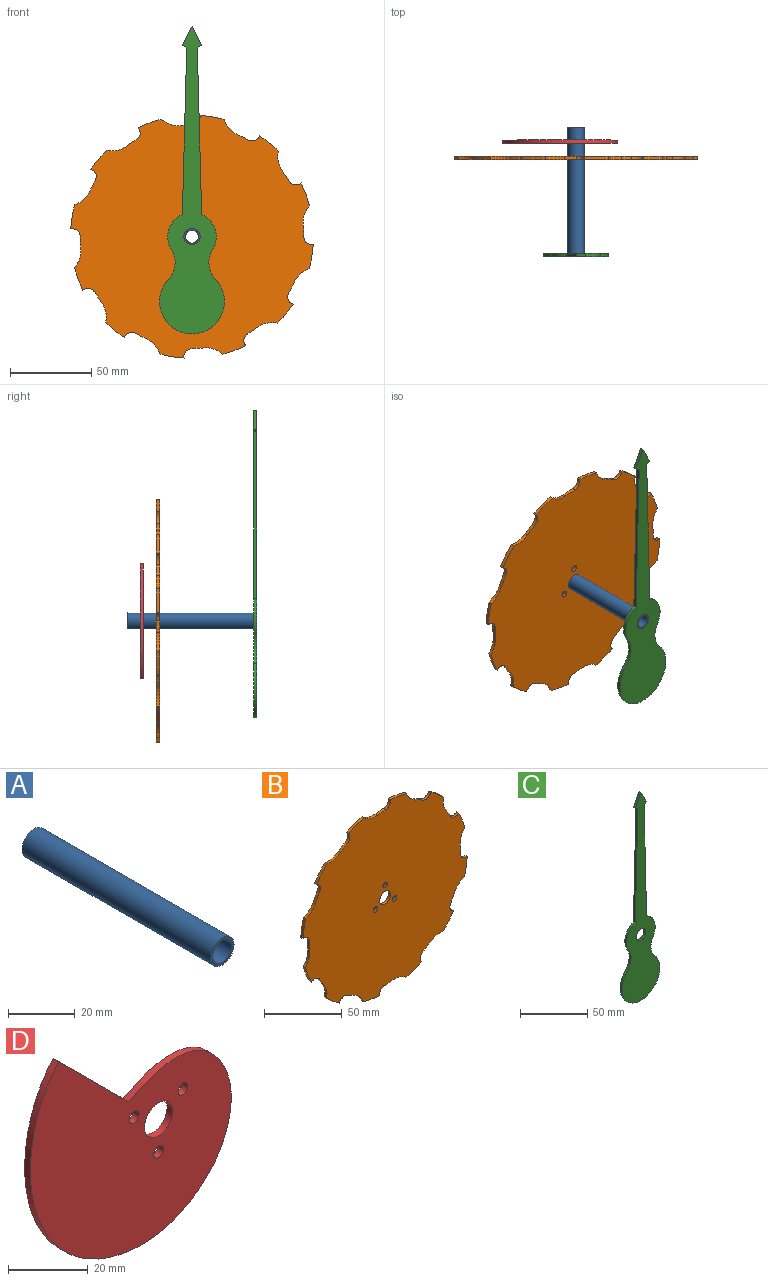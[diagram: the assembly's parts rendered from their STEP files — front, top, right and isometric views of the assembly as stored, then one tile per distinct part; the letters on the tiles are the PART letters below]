
ASSEMBLY  parts=4 mates=3
PART A: 4 faces, bbox 10x80x10 mm
  f0: cylinder r=4mm len=80mm, axis (0,1,0), area 2010.6mm2, adj f2,f3
  f1: cylinder r=5mm len=80mm, axis (0,1,0), area 2513.3mm2, adj f2,f3
  f2: plane 10x10mm, normal (0,-1,0), area 28.3mm2, adj f0,f1
  f3: plane 10x10mm, normal (0,1,0), area 28.3mm2, adj f0,f1
PART B: 54 faces, bbox 149.7x2x149.7 mm
  f0: cylinder r=75mm len=11.65mm, axis (0,1,0), area 30.3mm2, adj f13,f14,f47,f48
  f1: cylinder r=75mm len=14.9mm, axis (0,1,0), area 30.3mm2, adj f13,f14,f44,f45
  f2: cylinder r=75mm len=14.16mm, axis (0,1,0), area 30.3mm2, adj f13,f14,f41,f42
  f3: cylinder r=75mm len=11.65mm, axis (0,1,0), area 30.3mm2, adj f13,f14,f38,f39
  f4: cylinder r=75mm len=14.9mm, axis (0,1,0), area 30.3mm2, adj f13,f14,f35,f36
  f5: cylinder r=75mm len=14.16mm, axis (0,1,0), area 30.3mm2, adj f13,f14,f32,f33
  f6: cylinder r=75mm len=11.65mm, axis (0,1,0), area 30.3mm2, adj f13,f14,f29,f30
  f7: cylinder r=75mm len=14.9mm, axis (0,1,0), area 30.3mm2, adj f13,f14,f17,f27
  f8: cylinder r=75mm len=14.16mm, axis (0,1,0), area 30.3mm2, adj f13,f14,f24,f50
  f9: cylinder r=75mm len=14.9mm, axis (0,1,0), area 30.3mm2, adj f13,f14,f21,f26
  f10: cylinder r=75mm len=11.65mm, axis (0,1,0), area 30.3mm2, adj f13,f14,f18,f23
  f11: cylinder r=5mm len=10mm, axis (0,1,0), area 62.8mm2, adj f13,f14
  f12: cylinder r=75mm len=14.16mm, axis (0,1,0), area 30.3mm2, adj f13,f14,f15,f20
  f13: plane 149.68x149.68mm, normal (0,-1,0), area 16158.8mm2, adj f0,f1,f2,f3,f4,f5,f6,f7
  f14: plane 149.68x149.68mm, normal (0,1,0), area 16158.8mm2, adj f0,f1,f2,f3,f4,f5,f6,f7
  f15: cylinder r=15mm len=11.78mm, axis (0,-1,0), area 25.6mm2, adj f12,f13,f14,f16
  f16: cylinder r=69mm len=7.21mm, axis (0,-1,0), area 14.5mm2, adj f13,f14,f15,f17
  f17: cylinder r=5mm len=5.84mm, axis (0,-1,0), area 17.4mm2, adj f7,f13,f14,f16
  f18: cylinder r=15mm len=12.17mm, axis (0,-1,0), area 25.6mm2, adj f10,f13,f14,f19
  f19: cylinder r=69mm len=6.06mm, axis (0,-1,0), area 14.5mm2, adj f13,f14,f18,f20
  f20: cylinder r=5mm len=7.52mm, axis (0,-1,0), area 17.4mm2, adj f12,f13,f14,f19
  f21: cylinder r=15mm len=9.3mm, axis (0,-1,0), area 25.6mm2, adj f9,f13,f14,f22
  f22: cylinder r=69mm len=6.44mm, axis (0,-1,0), area 14.5mm2, adj f13,f14,f21,f23
  f23: cylinder r=5mm len=7.19mm, axis (0,-1,0), area 17.4mm2, adj f10,f13,f14,f22
  f24: cylinder r=15mm len=11.78mm, axis (0,-1,0), area 25.6mm2, adj f8,f13,f14,f25
  f25: cylinder r=69mm len=7.21mm, axis (0,-1,0), area 14.5mm2, adj f13,f14,f24,f26
  f26: cylinder r=5mm len=5.84mm, axis (0,-1,0), area 17.4mm2, adj f9,f13,f14,f25
  f27: cylinder r=15mm len=9.3mm, axis (0,-1,0), area 25.6mm2, adj f7,f13,f14,f28
  f28: cylinder r=69mm len=6.44mm, axis (0,-1,0), area 14.5mm2, adj f13,f14,f27,f29
  f29: cylinder r=5mm len=7.19mm, axis (0,-1,0), area 17.4mm2, adj f6,f13,f14,f28
  f30: cylinder r=15mm len=12.17mm, axis (0,-1,0), area 25.6mm2, adj f6,f13,f14,f31
  f31: cylinder r=69mm len=6.06mm, axis (0,-1,0), area 14.5mm2, adj f13,f14,f30,f32
  f32: cylinder r=5mm len=7.52mm, axis (0,-1,0), area 17.4mm2, adj f5,f13,f14,f31
  f33: cylinder r=15mm len=11.78mm, axis (0,-1,0), area 25.6mm2, adj f5,f13,f14,f34
  f34: cylinder r=69mm len=7.21mm, axis (0,-1,0), area 14.5mm2, adj f13,f14,f33,f35
  f35: cylinder r=5mm len=5.84mm, axis (0,-1,0), area 17.4mm2, adj f4,f13,f14,f34
  f36: cylinder r=15mm len=9.3mm, axis (0,-1,0), area 25.6mm2, adj f4,f13,f14,f37
  f37: cylinder r=69mm len=6.44mm, axis (0,-1,0), area 14.5mm2, adj f13,f14,f36,f38
  f38: cylinder r=5mm len=7.19mm, axis (0,-1,0), area 17.4mm2, adj f3,f13,f14,f37
  f39: cylinder r=15mm len=12.17mm, axis (0,-1,0), area 25.6mm2, adj f3,f13,f14,f40
  f40: cylinder r=69mm len=6.06mm, axis (0,-1,0), area 14.5mm2, adj f13,f14,f39,f41
  f41: cylinder r=5mm len=7.52mm, axis (0,-1,0), area 17.4mm2, adj f2,f13,f14,f40
  f42: cylinder r=15mm len=11.78mm, axis (0,-1,0), area 25.6mm2, adj f2,f13,f14,f43
  f43: cylinder r=69mm len=7.21mm, axis (0,-1,0), area 14.5mm2, adj f13,f14,f42,f44
  f44: cylinder r=5mm len=5.84mm, axis (0,-1,0), area 17.4mm2, adj f1,f13,f14,f43
  f45: cylinder r=15mm len=9.3mm, axis (0,-1,0), area 25.6mm2, adj f1,f13,f14,f46
  f46: cylinder r=69mm len=6.44mm, axis (0,-1,0), area 14.5mm2, adj f13,f14,f45,f47
  f47: cylinder r=5mm len=7.19mm, axis (0,-1,0), area 17.4mm2, adj f0,f13,f14,f46
  f48: cylinder r=15mm len=12.17mm, axis (0,-1,0), area 25.6mm2, adj f0,f13,f14,f49
  f49: cylinder r=69mm len=6.06mm, axis (0,-1,0), area 14.5mm2, adj f13,f14,f48,f50
  f50: cylinder r=5mm len=7.52mm, axis (0,-1,0), area 17.4mm2, adj f8,f13,f14,f49
  f51: cylinder r=2mm len=4mm, axis (0,-1,0), area 25.1mm2, adj f13,f14
  f52: cylinder r=2mm len=4mm, axis (0,-1,0), area 25.1mm2, adj f13,f14
  f53: cylinder r=2mm len=4mm, axis (0,-1,0), area 25.1mm2, adj f13,f14
PART C: 14 faces, bbox 40x2x190 mm
  f0: plane 2.69x2mm, normal (0.45,0,-0.89), area 6mm2, adj f1,f10,f12,f13
  f1: plane 11.91x5.95mm, normal (0.89,0,0.45), area 26.6mm2, adj f0,f2,f12,f13
  f2: plane 11.91x5.95mm, normal (-0.89,0,0.45), area 26.6mm2, adj f1,f3,f12,f13
  f3: plane 2.69x2mm, normal (-0.45,0,-0.89), area 6mm2, adj f2,f4,f12,f13
  f4: plane 102.98x2.69mm, normal (-1,0,0.03), area 206mm2, adj f3,f5,f12,f13
  f5: cylinder r=15mm len=21.74mm, axis (0,1,0), area 51.7mm2, adj f4,f6,f12,f13
  f6: cylinder r=15mm len=18.28mm, axis (0,1,0), area 39.5mm2, adj f5,f7,f12,f13
  f7: cylinder r=20mm len=40mm, axis (0,1,0), area 186.3mm2, adj f6,f8,f12,f13
  f8: cylinder r=15mm len=18.28mm, axis (0,1,0), area 39.5mm2, adj f7,f9,f12,f13
  f9: cylinder r=15mm len=21.74mm, axis (0,1,0), area 51.7mm2, adj f8,f10,f12,f13
  f10: plane 102.98x2.69mm, normal (1,0,0.03), area 206mm2, adj f0,f9,f12,f13
  f11: cylinder r=5mm len=10mm, axis (0,1,0), area 62.8mm2, adj f12,f13
  f12: plane 190x40mm, normal (0,-1,0), area 3073.4mm2, adj f0,f1,f2,f3,f4,f5,f6,f7
  f13: plane 190x40mm, normal (0,1,0), area 3073.4mm2, adj f0,f1,f2,f3,f4,f5,f6,f7
PART D: 8 faces, bbox 72.9x2x71.7 mm
  f0: extruded ~71.13x70.76mm, area 387.9mm2, adj f1,f3,f4
  f1: plane 24.75x24.75mm, normal (0.71,0,0.71), area 70mm2, adj f0,f3,f4
  f2: cylinder r=5mm len=10mm, axis (0,1,0), area 62.8mm2, adj f3,f4
  f3: plane 72.86x71.69mm, normal (0,-1,0), area 3161.4mm2, adj f0,f1,f2,f5,f6,f7
  f4: plane 72.86x71.69mm, normal (0,1,0), area 3161.4mm2, adj f0,f1,f2,f5,f6,f7
  f5: cylinder r=1.75mm len=3.5mm, axis (0,-1,0), area 22mm2, adj f3,f4
  f6: cylinder r=1.75mm len=3.5mm, axis (0,-1,0), area 22mm2, adj f3,f4
  f7: cylinder r=1.75mm len=3.5mm, axis (0,-1,0), area 22mm2, adj f3,f4
PLACE A t=(-97.18,35.5,-15.33)mm fixed
PLACE B t=(-97.18,17.5,-15.33)mm
PLACE C t=(-97.18,-42.5,-15.33)mm
PLACE D rot(axis=(1,0,0),180deg) t=(-97.18,25.5,-15.33)mm
MATE revolute A.f0 <-> B.f11  axis (0,1,0) through (-97.18,35.5,-15.33)mm
MATE revolute A.f1 <-> D.f2  axis (0,1,0) through (-97.18,35.5,-15.33)mm
MATE fastened C.f11 <-> A.f1  axis (0,-1,0) through (-97.18,-44.5,-15.33)mm
